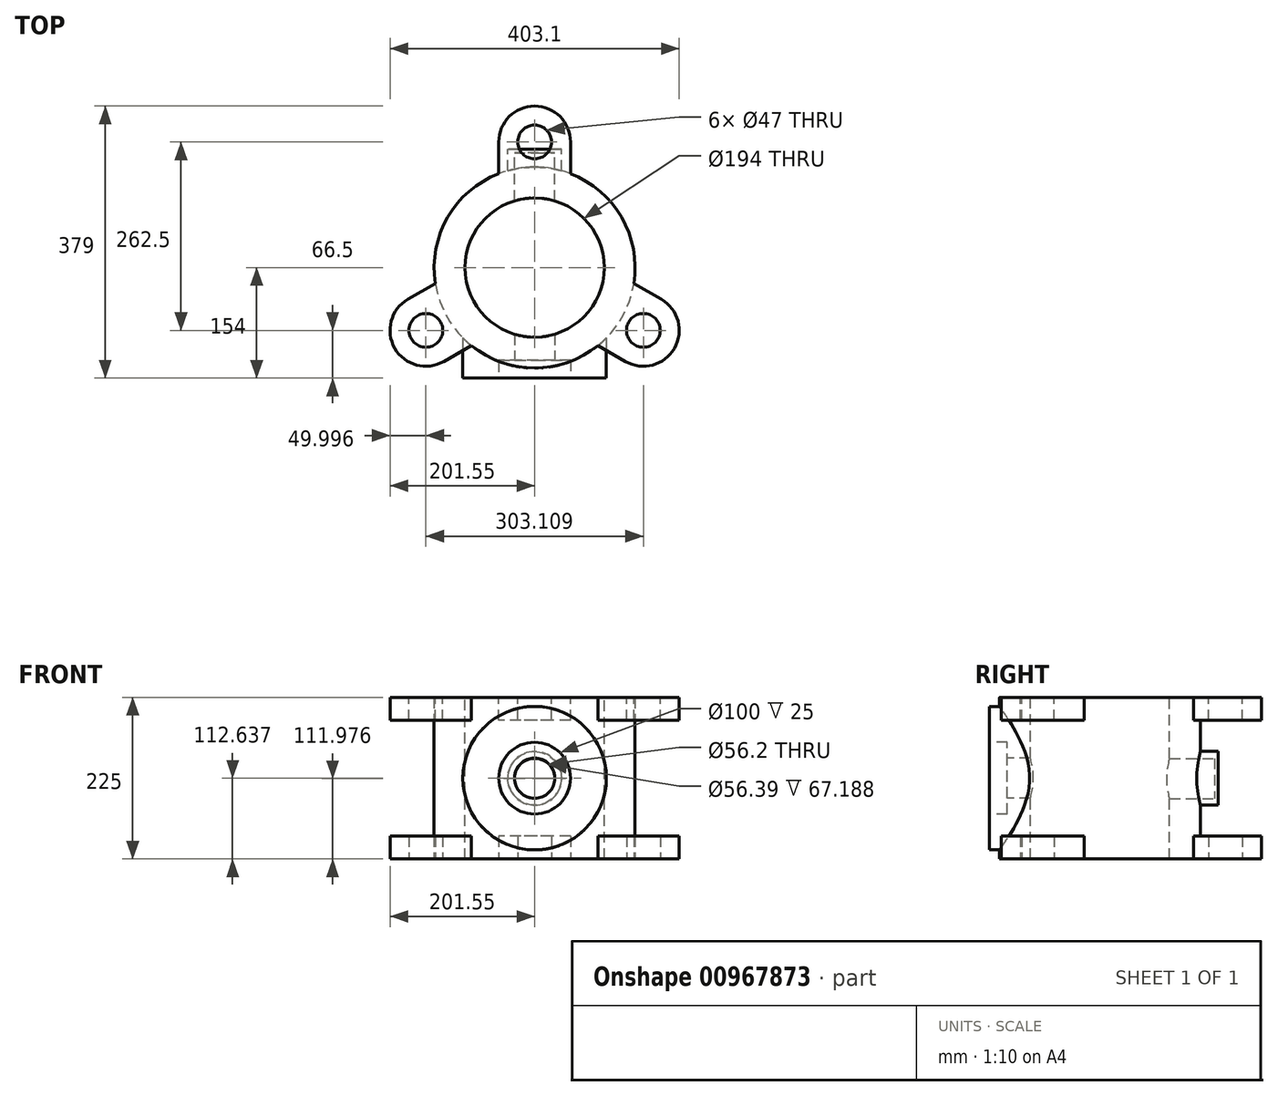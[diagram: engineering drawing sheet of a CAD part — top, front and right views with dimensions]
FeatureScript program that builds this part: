
annotation { "Feature Type Name" : "Feature", "Feature Type Description" : "" }
export const myFeature = defineFeature(function(context is Context, id is Id, definition is map)
    precondition{}
    {
        {
            var Q0;
            Q0=qCreatedBy(makeId("Top.planeOp"),FACE);
            var sketch = newSketch(context, id + "F0", { "sketchPlane" : qUnion([Q0])});
            skCircle(sketch, "E0", {"center": v(0, 0) * mm, "radius": 97 * mm});
            skArc(sketch, "E1", {"start": v(-50, 130.77) * mm, "mid": v(-121.24, 70) * mm, "end": v(-138.25, -22.08) * mm});
            skCircle(sketch, "E2", {"center": v(0, 0) * mm, "radius": 175 * mm, "construction": true});
            skLineSegment(sketch, "E3", {"start": v(0, 0) * mm, "end": v(0, 266.86) * mm, "construction": true});
            skCircle(sketch, "E4", {"center": v(0, 175) * mm, "radius": 23.5 * mm});
            skArc(sketch, "E5", {"start": v(50, 175) * mm, "mid": v(0, 225) * mm, "end": v(-50, 175) * mm});
            skLineSegment(sketch, "E6", {"start": v(-50, 175) * mm, "end": v(-50, 130.77) * mm});
            skLineSegment(sketch, "E7.MirrorCS", {"start": v(50, 175) * mm, "end": v(50, 130.77) * mm});
            skLineSegment(sketch, "E8.1.0", {"start": v(-176.55, -44.2) * mm, "end": v(-138.25, -22.08) * mm});
            skCircle(sketch, "E8.1.1", {"center": v(-151.55, -87.5) * mm, "radius": 23.5 * mm});
            skLineSegment(sketch, "E8.1.2", {"start": v(-126.55, -130.8) * mm, "end": v(-88.25, -108.68) * mm});
            skArc(sketch, "E8.1.3", {"start": v(-176.55, -44.2) * mm, "mid": v(-194.86, -112.5) * mm, "end": v(-126.55, -130.8) * mm});
            skLineSegment(sketch, "E8.2.0", {"start": v(126.55, -130.8) * mm, "end": v(88.25, -108.68) * mm});
            skCircle(sketch, "E8.2.1", {"center": v(151.55, -87.5) * mm, "radius": 23.5 * mm});
            skLineSegment(sketch, "E8.2.2", {"start": v(176.55, -44.2) * mm, "end": v(138.25, -22.08) * mm});
            skArc(sketch, "E8.2.3", {"start": v(126.55, -130.8) * mm, "mid": v(194.86, -112.5) * mm, "end": v(176.55, -44.2) * mm});
            skArc(sketch, "E9.trimOffspring", {"start": v(-88.25, -108.68) * mm, "mid": v(0, -140) * mm, "end": v(88.25, -108.68) * mm});
            skArc(sketch, "E10.trimOffspring", {"start": v(138.25, -22.08) * mm, "mid": v(121.24, 70) * mm, "end": v(50, 130.77) * mm});
            skSolve(sketch);
        }
        {
            var Q0;
            Q0 = qSketchRegion(id + "F0", true);
            extrude(context, id + "F1", {"entities" : qUnion([Q0]), "depth" : 32 * mm, "offsetDistance" : 25 * mm});
        }
        {
            var Q0;
            Q0=qCreatedBy(makeId("Top.planeOp"),FACE);
            cPlane(context, id + "F2", {"entities" : qUnion([Q0]), "cplaneType" : CPlaneType.OFFSET, "offset" : 225 * mm, "width" : 150 * mm, "height" : 150 * mm});
        }
        {
            var Q0;
            Q0=qCreatedBy(id+"F2.planeOp",FACE);
            var sketch = newSketch(context, id + "F3", { "sketchPlane" : qUnion([Q0])});
            skArc(sketch, "E11", {"start": v(-50, 130.77) * mm, "mid": v(-121.24, 70) * mm, "end": v(-138.25, -22.08) * mm});
            skCircle(sketch, "E12", {"center": v(0, 0) * mm, "radius": 97 * mm});
            skCircle(sketch, "E13", {"center": v(0, 0) * mm, "radius": 175 * mm, "construction": true});
            skLineSegment(sketch, "E14", {"start": v(0, 0) * mm, "end": v(0, 307.78) * mm, "construction": true});
            skCircle(sketch, "E15", {"center": v(0, 175) * mm, "radius": 23.5 * mm});
            skArc(sketch, "E16", {"start": v(50, 175) * mm, "mid": v(0, 225) * mm, "end": v(-50, 175) * mm});
            skLineSegment(sketch, "E17", {"start": v(-50, 175) * mm, "end": v(-50, 130.77) * mm});
            skLineSegment(sketch, "E18.MirrorCS", {"start": v(50, 175) * mm, "end": v(50, 130.77) * mm});
            skArc(sketch, "E19.1.0", {"start": v(-176.55, -44.2) * mm, "mid": v(-194.86, -112.5) * mm, "end": v(-126.55, -130.8) * mm});
            skCircle(sketch, "E19.1.1", {"center": v(-151.55, -87.5) * mm, "radius": 23.5 * mm});
            skLineSegment(sketch, "E19.1.2", {"start": v(-176.55, -44.2) * mm, "end": v(-138.25, -22.08) * mm});
            skLineSegment(sketch, "E19.1.3", {"start": v(-126.55, -130.8) * mm, "end": v(-88.25, -108.68) * mm});
            skArc(sketch, "E19.2.0", {"start": v(126.55, -130.8) * mm, "mid": v(194.86, -112.5) * mm, "end": v(176.55, -44.2) * mm});
            skCircle(sketch, "E19.2.1", {"center": v(151.55, -87.5) * mm, "radius": 23.5 * mm});
            skLineSegment(sketch, "E19.2.2", {"start": v(126.55, -130.8) * mm, "end": v(88.25, -108.68) * mm});
            skLineSegment(sketch, "E19.2.3", {"start": v(176.55, -44.2) * mm, "end": v(138.25, -22.08) * mm});
            skArc(sketch, "E20.trimOffspring", {"start": v(-88.25, -108.68) * mm, "mid": v(0, -140) * mm, "end": v(88.25, -108.68) * mm});
            skArc(sketch, "E21.trimOffspring", {"start": v(138.25, -22.08) * mm, "mid": v(121.24, 70) * mm, "end": v(50, 130.77) * mm});
            skSolve(sketch);
        }
        {
            var Q0;
            Q0 = qSketchRegion(id + "F3", true);
            extrude(context, id + "F4", {"entities" : qUnion([Q0]), "oppositeDirection" : true, "depth" : 32 * mm, "offsetDistance" : 25 * mm});
        }
        {
            var Q0;
            Q0=makeQuery(id+"F1.opExtrude","CAP_FACE",FACE,{"disambiguationData":[OSD([sQuery(id+"F0.wireOp",EDGE,"E0"),sQuery(id+"F0.wireOp",EDGE,"E1"),sQuery(id+"F0.wireOp",EDGE,"E4"),sQuery(id+"F0.wireOp",EDGE,"E5"),sQuery(id+"F0.wireOp",EDGE,"E6"),sQuery(id+"F0.wireOp",EDGE,"E7.MirrorCS"),sQuery(id+"F0.wireOp",EDGE,"E8.1.0"),sQuery(id+"F0.wireOp",EDGE,"E8.1.1"),sQuery(id+"F0.wireOp",EDGE,"E8.1.2"),sQuery(id+"F0.wireOp",EDGE,"E8.1.3"),sQuery(id+"F0.wireOp",EDGE,"E8.2.0"),sQuery(id+"F0.wireOp",EDGE,"E8.2.1"),sQuery(id+"F0.wireOp",EDGE,"E8.2.2"),sQuery(id+"F0.wireOp",EDGE,"E8.2.3"),sQuery(id+"F0.wireOp",EDGE,"E9.trimOffspring"),sQuery(id+"F0.wireOp",EDGE,"E10.trimOffspring")])],"isStart":false});
            var sketch = newSketch(context, id + "F5", { "sketchPlane" : qUnion([Q0])});
            skCircle(sketch, "E22", {"center": v(0, 0) * mm, "radius": 140 * mm});
            skSolve(sketch);
        }
        {
            var Q0;
            Q0 = qSketchRegion(id + "F5", true);
            var Q1;
            Q1=makeQuery(id+"F4.opExtrude","CAP_FACE",FACE,{"disambiguationData":[OSD([sQuery(id+"F3.wireOp",EDGE,"E11"),sQuery(id+"F3.wireOp",EDGE,"E12"),sQuery(id+"F3.wireOp",EDGE,"E15"),sQuery(id+"F3.wireOp",EDGE,"E16"),sQuery(id+"F3.wireOp",EDGE,"E17"),sQuery(id+"F3.wireOp",EDGE,"E18.MirrorCS"),sQuery(id+"F3.wireOp",EDGE,"E19.1.0"),sQuery(id+"F3.wireOp",EDGE,"E19.1.1"),sQuery(id+"F3.wireOp",EDGE,"E19.1.2"),sQuery(id+"F3.wireOp",EDGE,"E19.1.3"),sQuery(id+"F3.wireOp",EDGE,"E19.2.0"),sQuery(id+"F3.wireOp",EDGE,"E19.2.1"),sQuery(id+"F3.wireOp",EDGE,"E19.2.2"),sQuery(id+"F3.wireOp",EDGE,"E19.2.3"),sQuery(id+"F3.wireOp",EDGE,"E20.trimOffspring"),sQuery(id+"F3.wireOp",EDGE,"E21.trimOffspring")])],"isStart":false});
            extrude(context, id + "F6", {"entities" : qUnion([Q0]), "endBound" : BoundingType.UP_TO_SURFACE, "depth" : 25 * mm, "endBoundEntityFace" : qUnion([Q1]), "offsetDistance" : 25 * mm});
        }
        {
            var Q0;
            Q0=makeQuery(id+"F6.opExtrude","CAP_FACE",FACE,{"disambiguationData":[OSD([sQuery(id+"F5.wireOp",EDGE,"E22")])],"isStart":false});
            var sketch = newSketch(context, id + "F7", { "sketchPlane" : qUnion([Q0])});
            skCircle(sketch, "E23", {"center": v(0, 0) * mm, "radius": 97 * mm});
            skSolve(sketch);
        }
        {
            var Q0;
            Q0 = qSketchRegion(id + "F7", true);
            extrude(context, id + "F8", {"entities" : qUnion([Q0]), "operationType" : NewBodyOperationType.REMOVE, "endBound" : BoundingType.THROUGH_ALL, "oppositeDirection" : true, "depth" : 25 * mm, "offsetDistance" : 25 * mm});
        }
        {
            var Q0;
            Q0=makeQuery(id+"F6.opExtrude","SWEPT_BODY",BODY,{"disambiguationData":[OSD([sQuery(id+"F5.wireOp",EDGE,"E22")])]});
            var Q1;
            Q1=makeQuery(id+"F1.opExtrude","SWEPT_BODY",BODY,{"disambiguationData":[OSD([sQuery(id+"F0.wireOp",EDGE,"E0"),sQuery(id+"F0.wireOp",EDGE,"E1"),sQuery(id+"F0.wireOp",EDGE,"E4"),sQuery(id+"F0.wireOp",EDGE,"E5"),sQuery(id+"F0.wireOp",EDGE,"E6"),sQuery(id+"F0.wireOp",EDGE,"E7.MirrorCS"),sQuery(id+"F0.wireOp",EDGE,"E8.1.0"),sQuery(id+"F0.wireOp",EDGE,"E8.1.1"),sQuery(id+"F0.wireOp",EDGE,"E8.1.2"),sQuery(id+"F0.wireOp",EDGE,"E8.1.3"),sQuery(id+"F0.wireOp",EDGE,"E8.2.0"),sQuery(id+"F0.wireOp",EDGE,"E8.2.1"),sQuery(id+"F0.wireOp",EDGE,"E8.2.2"),sQuery(id+"F0.wireOp",EDGE,"E8.2.3"),sQuery(id+"F0.wireOp",EDGE,"E9.trimOffspring"),sQuery(id+"F0.wireOp",EDGE,"E10.trimOffspring")])]});
            booleanBodies(context, id + "F9", {"operationType" : BooleanOperationType.UNION, "tools" : qUnion([Q0, Q1])});
        }
        {
            var Q0;
            Q0=makeQuery(id+"F6.opExtrude","SWEPT_BODY",BODY,{"disambiguationData":[OSD([sQuery(id+"F5.wireOp",EDGE,"E22")])]});
            var Q1;
            Q1=makeQuery(id+"F4.opExtrude","SWEPT_BODY",BODY,{"disambiguationData":[OSD([sQuery(id+"F3.wireOp",EDGE,"E11"),sQuery(id+"F3.wireOp",EDGE,"E12"),sQuery(id+"F3.wireOp",EDGE,"E15"),sQuery(id+"F3.wireOp",EDGE,"E16"),sQuery(id+"F3.wireOp",EDGE,"E17"),sQuery(id+"F3.wireOp",EDGE,"E18.MirrorCS"),sQuery(id+"F3.wireOp",EDGE,"E19.1.0"),sQuery(id+"F3.wireOp",EDGE,"E19.1.1"),sQuery(id+"F3.wireOp",EDGE,"E19.1.2"),sQuery(id+"F3.wireOp",EDGE,"E19.1.3"),sQuery(id+"F3.wireOp",EDGE,"E19.2.0"),sQuery(id+"F3.wireOp",EDGE,"E19.2.1"),sQuery(id+"F3.wireOp",EDGE,"E19.2.2"),sQuery(id+"F3.wireOp",EDGE,"E19.2.3"),sQuery(id+"F3.wireOp",EDGE,"E20.trimOffspring"),sQuery(id+"F3.wireOp",EDGE,"E21.trimOffspring")])]});
            booleanBodies(context, id + "F10", {"operationType" : BooleanOperationType.UNION, "tools" : qUnion([Q0, Q1])});
        }
        {
            var Q0;
            Q0=qCreatedBy(makeId("Front.planeOp"),FACE);
            cPlane(context, id + "F11", {"entities" : qUnion([Q0]), "cplaneType" : CPlaneType.OFFSET, "offset" : 154 * mm, "width" : 150 * mm, "height" : 150 * mm});
        }
        {
            var Q0;
            Q0=qCreatedBy(id+"F11.planeOp",FACE);
            var sketch = newSketch(context, id + "F12", { "sketchPlane" : qUnion([Q0])});
            skCircle(sketch, "E24", {"center": v(0, 112.64) * mm, "radius": 100 * mm});
            skSolve(sketch);
        }
        {
            var Q0;
            Q0=makeQuery(id+"F12.imprint","IMPRINT",FACE,{"disambiguationData":[TD([[makeQuery(id+"F12.imprint","IMPRINT",EDGE,{"derivedFrom":sQuery(id+"F12.wireOp",EDGE,"E24")}),1.0]])]});
            var Q1;
            Q1=makeQuery(id+"F10.opBoolean","MERGE",FACE,{"derivedFrom":[makeQuery(id+"F4.opExtrude","SWEPT_FACE",FACE,{"disambiguationData":[OSD([sQuery(id+"F3.wireOp",EDGE,"E11")])]}),makeQuery(id+"F4.opExtrude","SWEPT_FACE",FACE,{"disambiguationData":[OSD([sQuery(id+"F3.wireOp",EDGE,"E20.trimOffspring")])]}),makeQuery(id+"F4.opExtrude","SWEPT_FACE",FACE,{"disambiguationData":[OSD([sQuery(id+"F3.wireOp",EDGE,"E21.trimOffspring")])]}),makeQuery(id+"F9.opBoolean","MERGE",FACE,{"derivedFrom":[makeQuery(id+"F1.opExtrude","SWEPT_FACE",FACE,{"disambiguationData":[OSD([sQuery(id+"F0.wireOp",EDGE,"E1")])]}),makeQuery(id+"F1.opExtrude","SWEPT_FACE",FACE,{"disambiguationData":[OSD([sQuery(id+"F0.wireOp",EDGE,"E9.trimOffspring")])]}),makeQuery(id+"F1.opExtrude","SWEPT_FACE",FACE,{"disambiguationData":[OSD([sQuery(id+"F0.wireOp",EDGE,"E10.trimOffspring")])]}),makeQuery(id+"F6.opExtrude","SWEPT_FACE",FACE,{"disambiguationData":[OSD([sQuery(id+"F5.wireOp",EDGE,"E22")])]})]})]});
            extrude(context, id + "F13", {"entities" : qUnion([Q0]), "operationType" : NewBodyOperationType.ADD, "endBound" : BoundingType.UP_TO_SURFACE, "oppositeDirection" : true, "depth" : 25 * mm, "endBoundEntityFace" : qUnion([Q1]), "offsetDistance" : 25 * mm});
        }
        {
            var Q0;
            Q0=makeQuery(id+"F13.opExtrude","CAP_FACE",FACE,{"disambiguationData":[OSD([sQuery(id+"F12.wireOp",EDGE,"E24")])],"isStart":true});
            var sketch = newSketch(context, id + "F14", { "sketchPlane" : qUnion([Q0])});
            skCircle(sketch, "E25", {"center": v(0, 112.64) * mm, "radius": 50 * mm});
            skSolve(sketch);
        }
        {
            var Q0;
            Q0 = qSketchRegion(id + "F14", true);
            extrude(context, id + "F15", {"entities" : qUnion([Q0]), "operationType" : NewBodyOperationType.REMOVE, "oppositeDirection" : true, "depth" : 25 * mm, "offsetDistance" : 25 * mm});
        }
        {
            var Q0;
            Q0=makeQuery(id+"F15.boolean.opBoolean","COPY",FACE,{"derivedFrom":makeQuery(id+"F15.opExtrude","CAP_FACE",FACE,{"disambiguationData":[OSD([sQuery(id+"F14.wireOp",EDGE,"E25")])],"isStart":false})});
            var sketch = newSketch(context, id + "F16", { "sketchPlane" : qUnion([Q0])});
            skCircle(sketch, "E26", {"center": v(0, 112.64) * mm, "radius": 28.1 * mm});
            skSolve(sketch);
        }
        {
            var Q0;
            Q0 = qSketchRegion(id + "F16", true);
            extrude(context, id + "F17", {"entities" : qUnion([Q0]), "operationType" : NewBodyOperationType.REMOVE, "oppositeDirection" : true, "depth" : 45 * mm, "offsetDistance" : 25 * mm});
        }
        {
            var Q0;
            Q0=qCreatedBy(makeId("Front.planeOp"),FACE);
            cPlane(context, id + "F18", {"entities" : qUnion([Q0]), "cplaneType" : CPlaneType.OFFSET, "offset" : 165 * mm, "oppositeDirection" : true, "width" : 150 * mm, "height" : 150 * mm});
        }
        {
            var Q0;
            Q0=qCreatedBy(id+"F18.planeOp",FACE);
            var sketch = newSketch(context, id + "F19", { "sketchPlane" : qUnion([Q0])});
            skCircle(sketch, "E27", {"center": v(0, 112.36) * mm, "radius": 37.5 * mm});
            skSolve(sketch);
        }
        {
            var Q0;
            Q0 = qSketchRegion(id + "F19", true);
            var Q1;
            Q1=makeQuery(id+"F10.opBoolean","MERGE",FACE,{"derivedFrom":[makeQuery(id+"F4.opExtrude","SWEPT_FACE",FACE,{"disambiguationData":[OSD([sQuery(id+"F3.wireOp",EDGE,"E11")])]}),makeQuery(id+"F4.opExtrude","SWEPT_FACE",FACE,{"disambiguationData":[OSD([sQuery(id+"F3.wireOp",EDGE,"E20.trimOffspring")])]}),makeQuery(id+"F4.opExtrude","SWEPT_FACE",FACE,{"disambiguationData":[OSD([sQuery(id+"F3.wireOp",EDGE,"E21.trimOffspring")])]}),makeQuery(id+"F9.opBoolean","MERGE",FACE,{"derivedFrom":[makeQuery(id+"F1.opExtrude","SWEPT_FACE",FACE,{"disambiguationData":[OSD([sQuery(id+"F0.wireOp",EDGE,"E1")])]}),makeQuery(id+"F1.opExtrude","SWEPT_FACE",FACE,{"disambiguationData":[OSD([sQuery(id+"F0.wireOp",EDGE,"E9.trimOffspring")])]}),makeQuery(id+"F1.opExtrude","SWEPT_FACE",FACE,{"disambiguationData":[OSD([sQuery(id+"F0.wireOp",EDGE,"E10.trimOffspring")])]}),makeQuery(id+"F6.opExtrude","SWEPT_FACE",FACE,{"disambiguationData":[OSD([sQuery(id+"F5.wireOp",EDGE,"E22")])]})]})]});
            extrude(context, id + "F20", {"entities" : qUnion([Q0]), "operationType" : NewBodyOperationType.ADD, "endBound" : BoundingType.UP_TO_SURFACE, "depth" : 25 * mm, "endBoundEntityFace" : qUnion([Q1]), "offsetDistance" : 25 * mm});
        }
        {
            var Q0;
            Q0=makeQuery(id+"F20.opExtrude","CAP_FACE",FACE,{"disambiguationData":[OSD([sQuery(id+"F19.wireOp",EDGE,"E27")])],"isStart":true});
            cPlane(context, id + "F21", {"entities" : qUnion([Q0]), "cplaneType" : CPlaneType.OFFSET, "offset" : 5 * mm, "oppositeDirection" : true, "width" : 150 * mm, "height" : 150 * mm});
        }
        {
            var Q0;
            Q0=qCreatedBy(id+"F21.planeOp",FACE);
            var sketch = newSketch(context, id + "F22", { "sketchPlane" : qUnion([Q0])});
            skCircle(sketch, "E28", {"center": v(0, 111.98) * mm, "radius": 28.2 * mm});
            skSolve(sketch);
        }
        {
            var Q0;
            Q0 = qSketchRegion(id + "F22", true);
            extrude(context, id + "F23", {"entities" : qUnion([Q0]), "operationType" : NewBodyOperationType.REMOVE, "oppositeDirection" : true, "depth" : 75 * mm, "offsetDistance" : 25 * mm});
        }
    });
